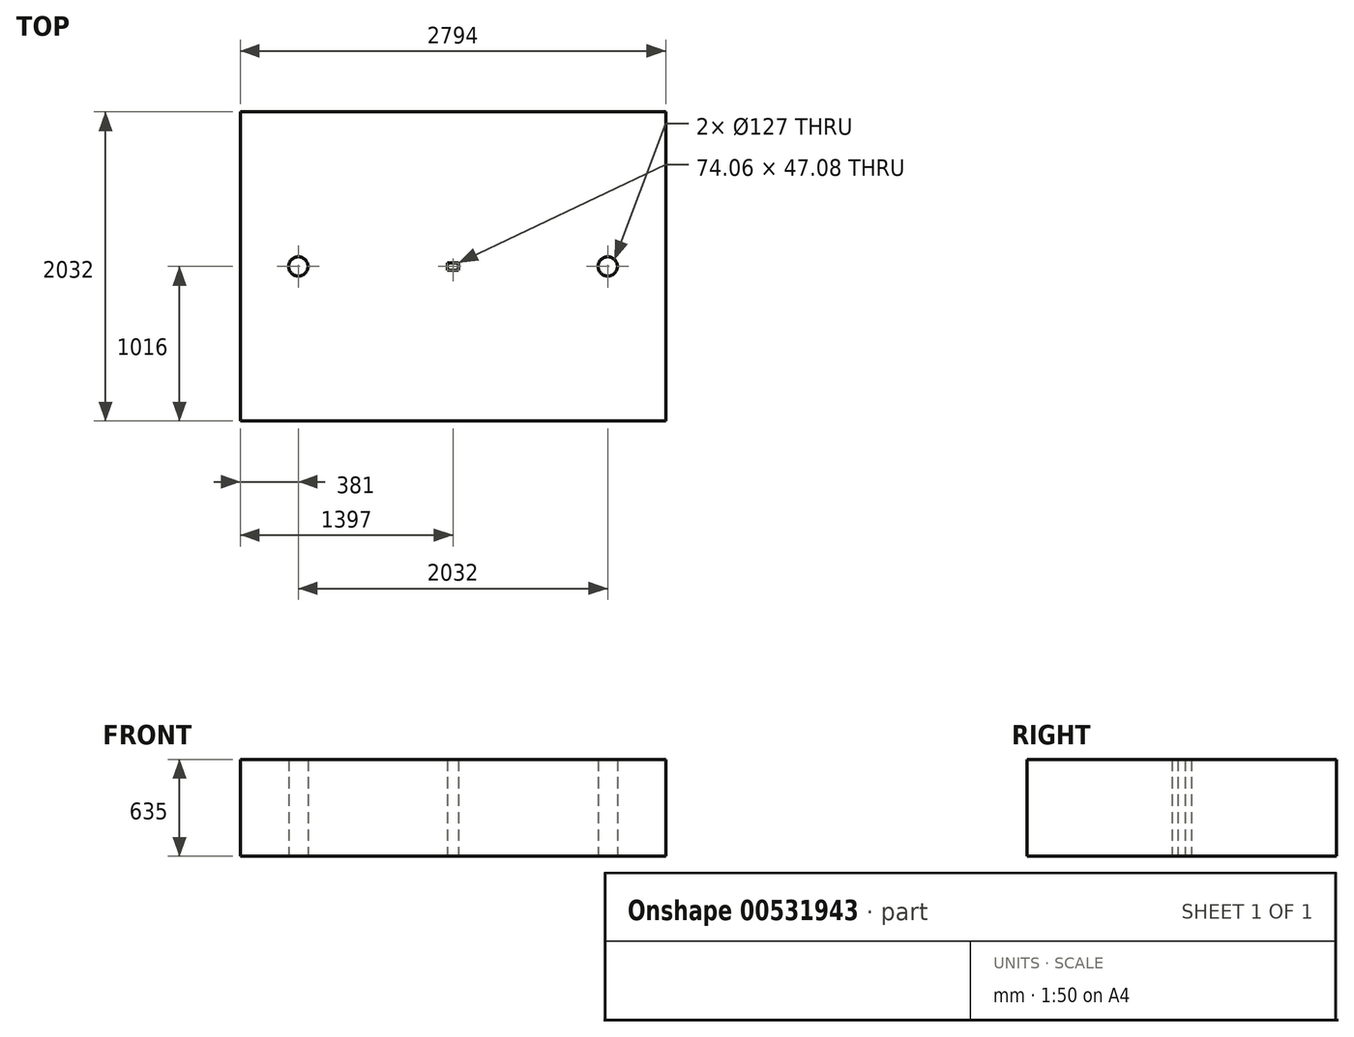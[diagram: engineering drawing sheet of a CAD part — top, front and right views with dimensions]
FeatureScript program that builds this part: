
annotation { "Feature Type Name" : "Feature", "Feature Type Description" : "" }
export const myFeature = defineFeature(function(context is Context, id is Id, definition is map)
    precondition{}
    {
        {
            var Q0;
            Q0=qCreatedBy(makeId("Top.planeOp"),FACE);
            var sketch = newSketch(context, id + "F0", { "sketchPlane" : qUnion([Q0])});
            skLineSegment(sketch, "E0.bottom", {"start": v(-1397, -1016) * mm, "end": v(1397, -1016) * mm});
            skLineSegment(sketch, "E0.top", {"start": v(-1397, 1016) * mm, "end": v(1397, 1016) * mm});
            skLineSegment(sketch, "E0.left", {"start": v(-1397, -1016) * mm, "end": v(-1397, 1016) * mm});
            skLineSegment(sketch, "E0.right", {"start": v(1397, -1016) * mm, "end": v(1397, 1016) * mm});
            skPoint(sketch, "E0.middle", {"position": v(0, 0) * mm});
            skCircle(sketch, "E1", {"center": v(-1016, 0) * mm, "radius": 63.5 * mm});
            skCircle(sketch, "E2", {"center": v(1016, 0) * mm, "radius": 63.5 * mm});
            skLineSegment(sketch, "E3.bottom", {"start": v(-37.03, -23.54) * mm, "end": v(37.03, -23.54) * mm});
            skLineSegment(sketch, "E3.top", {"start": v(-37.03, 23.54) * mm, "end": v(37.03, 23.54) * mm});
            skLineSegment(sketch, "E3.left", {"start": v(-37.03, -23.54) * mm, "end": v(-37.03, 23.54) * mm});
            skLineSegment(sketch, "E3.right", {"start": v(37.03, -23.54) * mm, "end": v(37.03, 23.54) * mm});
            skSolve(sketch);
        }
        {
            var Q0;
            Q0=makeQuery(id+"F0.imprint","IMPRINT",FACE,{"disambiguationData":[TD([[makeQuery(id+"F0.imprint","IMPRINT",EDGE,{"derivedFrom":sQuery(id+"F0.wireOp",EDGE,"E0.bottom")}),1.0]])]});
            extrude(context, id + "F1", {"entities" : qUnion([Q0]), "depth" : 635 * mm, "offsetDistance" : 25.4 * mm});
        }
    });
